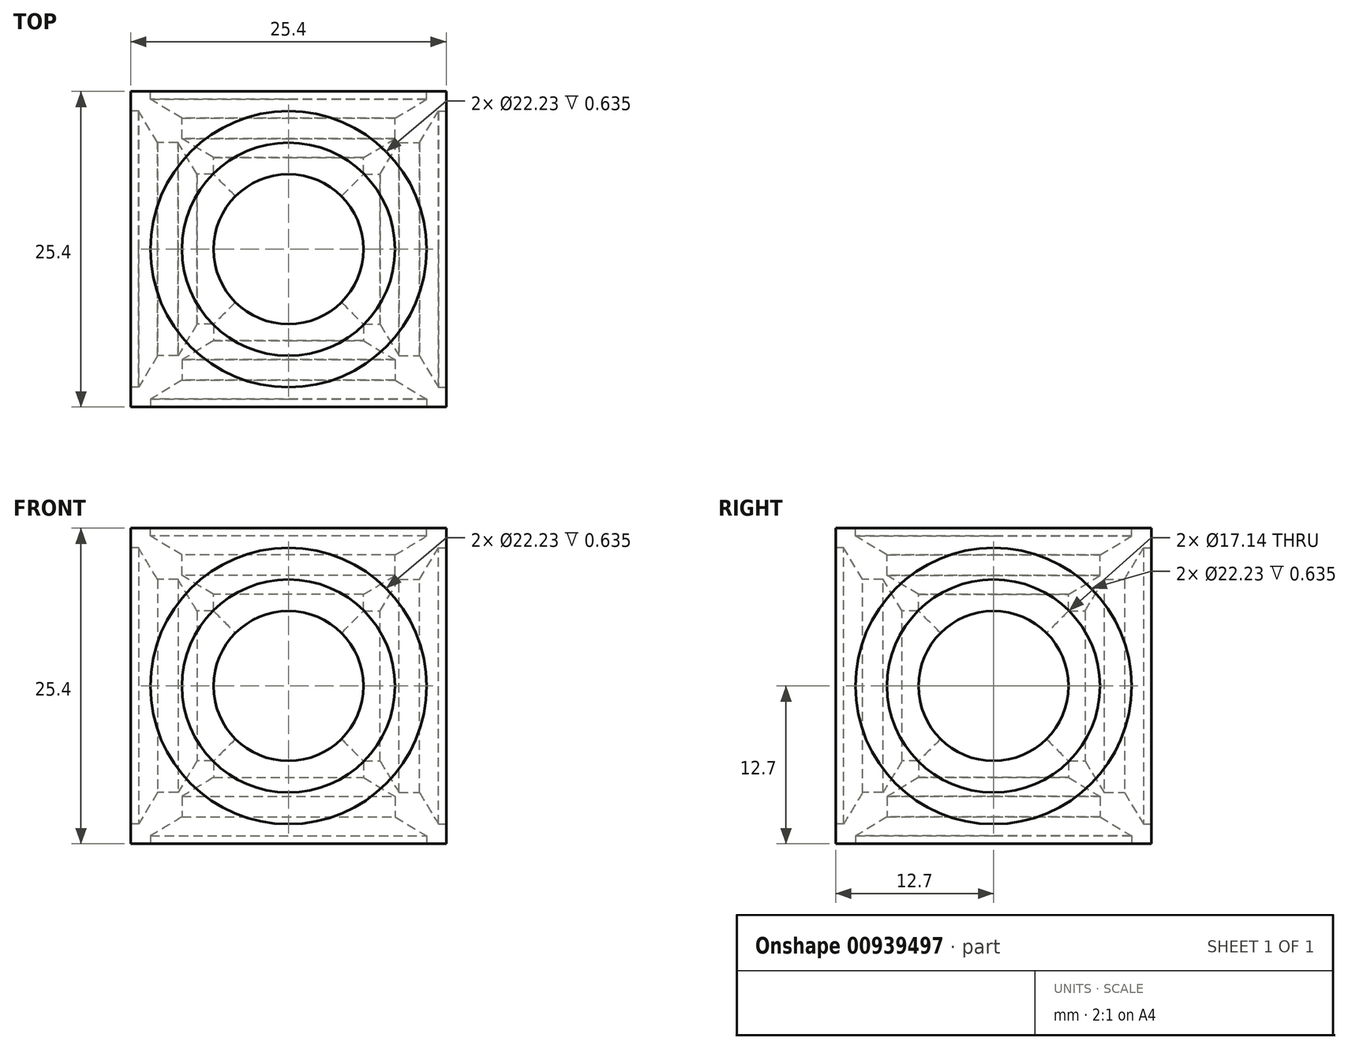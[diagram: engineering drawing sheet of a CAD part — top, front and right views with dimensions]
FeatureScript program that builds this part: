
annotation { "Feature Type Name" : "Feature", "Feature Type Description" : "" }
export const myFeature = defineFeature(function(context is Context, id is Id, definition is map)
    precondition{}
    {
        {
            var Q0;
            Q0=qCreatedBy(makeId("Top.planeOp"),FACE);
            var sketch = newSketch(context, id + "F0", { "sketchPlane" : qUnion([Q0])});
            skLineSegment(sketch, "E0.bottom", {"start": v(12.7, 12.7) * mm, "end": v(-12.7, 12.7) * mm});
            skLineSegment(sketch, "E0.top", {"start": v(12.7, -12.7) * mm, "end": v(-12.7, -12.7) * mm});
            skLineSegment(sketch, "E0.left", {"start": v(12.7, 12.7) * mm, "end": v(12.7, -12.7) * mm});
            skLineSegment(sketch, "E0.right", {"start": v(-12.7, 12.7) * mm, "end": v(-12.7, -12.7) * mm});
            skPoint(sketch, "E0.middle", {"position": v(0, 0) * mm});
            skSolve(sketch);
        }
        {
            var Q0;
            Q0 = qSketchRegion(id + "F0", true);
            extrude(context, id + "F1", {"entities" : qUnion([Q0]), "endBound" : BoundingType.SYMMETRIC, "depth" : 25.4 * mm, "offsetDistance" : 25.4 * mm});
        }
        {
            var Q0;
            Q0=makeQuery(id+"F1.opExtrude","CAP_FACE",FACE,{"disambiguationData":[OSD([sQuery(id+"F0.wireOp",EDGE,"E0.bottom"),sQuery(id+"F0.wireOp",EDGE,"E0.top"),sQuery(id+"F0.wireOp",EDGE,"E0.left"),sQuery(id+"F0.wireOp",EDGE,"E0.right")])],"isStart":false});
            var sketch = newSketch(context, id + "F2", { "sketchPlane" : qUnion([Q0])});
            skPoint(sketch, "E1", {"position": v(0, 0) * mm});
            skSolve(sketch);
        }
        {
            var Q0;
            Q0=sQuery(id+"F2.wireOp",VERTEX,"E1");
            var Q1;
            Q1=makeQuery(id+"F1.opExtrude","SWEPT_BODY",BODY,{"disambiguationData":[OSD([sQuery(id+"F0.wireOp",EDGE,"E0.bottom"),sQuery(id+"F0.wireOp",EDGE,"E0.top"),sQuery(id+"F0.wireOp",EDGE,"E0.left"),sQuery(id+"F0.wireOp",EDGE,"E0.right")])]});
            hole(context, id + "F3", {"style" : HoleStyle.SIMPLE, "endStyle" : HoleEndStyle.THROUGH, "holeDiameter" : 3.17 * mm, "majorDiameter" : 6.35 * mm, "isTappedThrough" : true, "tappedDepth" : 12.7 * mm, "tapClearance" : 3, "locations" : qUnion([Q0]), "scope" : qUnion([Q1])});
        }
        {
            var Q0;
            Q0=makeQuery(id+"F1.opExtrude","SWEPT_FACE",FACE,{"disambiguationData":[OSD([sQuery(id+"F0.wireOp",EDGE,"E0.right")])]});
            var sketch = newSketch(context, id + "F4", { "sketchPlane" : qUnion([Q0])});
            skPoint(sketch, "E2", {"position": v(0, 0) * mm});
            skSolve(sketch);
        }
        {
            var Q0;
            Q0=sQuery(id+"F4.wireOp",VERTEX,"E2");
            var Q1;
            Q1=makeQuery(id+"F1.opExtrude","SWEPT_BODY",BODY,{"disambiguationData":[OSD([sQuery(id+"F0.wireOp",EDGE,"E0.bottom"),sQuery(id+"F0.wireOp",EDGE,"E0.top"),sQuery(id+"F0.wireOp",EDGE,"E0.left"),sQuery(id+"F0.wireOp",EDGE,"E0.right")])]});
            hole(context, id + "F5", {"style" : HoleStyle.SIMPLE, "endStyle" : HoleEndStyle.THROUGH, "holeDiameter" : 3.17 * mm, "majorDiameter" : 6.35 * mm, "isTappedThrough" : true, "tappedDepth" : 12.7 * mm, "tapClearance" : 3, "locations" : qUnion([Q0]), "scope" : qUnion([Q1])});
        }
        {
            var Q0;
            Q0=makeQuery(id+"F1.opExtrude","SWEPT_FACE",FACE,{"disambiguationData":[OSD([sQuery(id+"F0.wireOp",EDGE,"E0.bottom")])]});
            var sketch = newSketch(context, id + "F6", { "sketchPlane" : qUnion([Q0])});
            skPoint(sketch, "E3", {"position": v(0, 0) * mm});
            skSolve(sketch);
        }
        {
            var Q0;
            Q0=sQuery(id+"F6.wireOp",VERTEX,"E3");
            var Q1;
            Q1=makeQuery(id+"F1.opExtrude","SWEPT_BODY",BODY,{"disambiguationData":[OSD([sQuery(id+"F0.wireOp",EDGE,"E0.bottom"),sQuery(id+"F0.wireOp",EDGE,"E0.top"),sQuery(id+"F0.wireOp",EDGE,"E0.left"),sQuery(id+"F0.wireOp",EDGE,"E0.right")])]});
            hole(context, id + "F7", {"style" : HoleStyle.SIMPLE, "endStyle" : HoleEndStyle.THROUGH, "holeDiameter" : 3.17 * mm, "majorDiameter" : 6.35 * mm, "isTappedThrough" : true, "tappedDepth" : 12.7 * mm, "tapClearance" : 3, "locations" : qUnion([Q0]), "scope" : qUnion([Q1])});
        }
        {
            var Q0;
            Q0=makeQuery(id+"F1.opExtrude","CAP_FACE",FACE,{"disambiguationData":[OSD([sQuery(id+"F0.wireOp",EDGE,"E0.bottom"),sQuery(id+"F0.wireOp",EDGE,"E0.top"),sQuery(id+"F0.wireOp",EDGE,"E0.left"),sQuery(id+"F0.wireOp",EDGE,"E0.right")])],"isStart":true});
            var sketch = newSketch(context, id + "F8", { "sketchPlane" : qUnion([Q0])});
            skPoint(sketch, "E4", {"position": v(0, 0) * mm});
            skSolve(sketch);
        }
        {
            var Q0;
            Q0=makeQuery(id+"F1.opExtrude","SWEPT_FACE",FACE,{"disambiguationData":[OSD([sQuery(id+"F0.wireOp",EDGE,"E0.left")])]});
            var sketch = newSketch(context, id + "F9", { "sketchPlane" : qUnion([Q0])});
            skPoint(sketch, "E5", {"position": v(0, 0) * mm});
            skSolve(sketch);
        }
        {
            var Q0;
            Q0=makeQuery(id+"F1.opExtrude","SWEPT_FACE",FACE,{"disambiguationData":[OSD([sQuery(id+"F0.wireOp",EDGE,"E0.top")])]});
            var sketch = newSketch(context, id + "F10", { "sketchPlane" : qUnion([Q0])});
            skPoint(sketch, "E6", {"position": v(0, 0) * mm});
            skSolve(sketch);
        }
        {
            var Q0;
            Q0=sQuery(id+"F8.wireOp",VERTEX,"E4");
            var Q1;
            Q1=sQuery(id+"F6.wireOp",VERTEX,"E3");
            var Q2;
            Q2=sQuery(id+"F10.wireOp",VERTEX,"E6");
            var Q3;
            Q3=sQuery(id+"F4.wireOp",VERTEX,"E2");
            var Q4;
            Q4=sQuery(id+"F9.wireOp",VERTEX,"E5");
            var Q5;
            Q5=sQuery(id+"F2.wireOp",VERTEX,"E1");
            var Q6;
            Q6=makeQuery(id+"F1.opExtrude","SWEPT_BODY",BODY,{"disambiguationData":[OSD([sQuery(id+"F0.wireOp",EDGE,"E0.bottom"),sQuery(id+"F0.wireOp",EDGE,"E0.top"),sQuery(id+"F0.wireOp",EDGE,"E0.left"),sQuery(id+"F0.wireOp",EDGE,"E0.right")])]});
            hole(context, id + "F11", {"style" : HoleStyle.SIMPLE, "endStyle" : HoleEndStyle.BLIND, "holeDiameter" : 17.14 * mm, "majorDiameter" : 6.35 * mm, "holeDepth" : 3.8 * mm, "isTappedThrough" : true, "tappedDepth" : 12.7 * mm, "tapClearance" : 3, "locations" : qUnion([Q0, Q1, Q2, Q3, Q4, Q5]), "scope" : qUnion([Q6])});
        }
        {
            var Q0;
            Q0=sQuery(id+"F9.wireOp",VERTEX,"E5");
            var Q1;
            Q1=sQuery(id+"F2.wireOp",VERTEX,"E1");
            var Q2;
            Q2=sQuery(id+"F10.wireOp",VERTEX,"E6");
            var Q3;
            Q3=sQuery(id+"F8.wireOp",VERTEX,"E4");
            var Q4;
            Q4=sQuery(id+"F4.wireOp",VERTEX,"E2");
            var Q5;
            Q5=sQuery(id+"F6.wireOp",VERTEX,"E3");
            var Q6;
            Q6=makeQuery(id+"F1.opExtrude","SWEPT_BODY",BODY,{"disambiguationData":[OSD([sQuery(id+"F0.wireOp",EDGE,"E0.bottom"),sQuery(id+"F0.wireOp",EDGE,"E0.top"),sQuery(id+"F0.wireOp",EDGE,"E0.left"),sQuery(id+"F0.wireOp",EDGE,"E0.right")])]});
            hole(context, id + "F12", {"style" : HoleStyle.SIMPLE, "endStyle" : HoleEndStyle.BLIND, "holeDiameter" : 22.22 * mm, "majorDiameter" : 6.35 * mm, "holeDepth" : 0.64 * mm, "isTappedThrough" : true, "tappedDepth" : 12.7 * mm, "tapClearance" : 3, "locations" : qUnion([Q0, Q1, Q2, Q3, Q4, Q5]), "scope" : qUnion([Q6])});
        }
        {
            var Q0;
            Q0=sQuery(id+"F4.wireOp",VERTEX,"E2");
            var Q1;
            Q1=sQuery(id+"F8.wireOp",VERTEX,"E4");
            var Q2;
            Q2=sQuery(id+"F10.wireOp",VERTEX,"E6");
            var Q3;
            Q3=sQuery(id+"F9.wireOp",VERTEX,"E5");
            var Q4;
            Q4=sQuery(id+"F6.wireOp",VERTEX,"E3");
            var Q5;
            Q5=sQuery(id+"F2.wireOp",VERTEX,"E1");
            var Q6;
            Q6=makeQuery(id+"F1.opExtrude","SWEPT_BODY",BODY,{"disambiguationData":[OSD([sQuery(id+"F0.wireOp",EDGE,"E0.bottom"),sQuery(id+"F0.wireOp",EDGE,"E0.top"),sQuery(id+"F0.wireOp",EDGE,"E0.left"),sQuery(id+"F0.wireOp",EDGE,"E0.right")])]});
            hole(context, id + "F13", {"style" : HoleStyle.SIMPLE, "endStyle" : HoleEndStyle.BLIND, "holeDiameter" : 12.06 * mm, "majorDiameter" : 6.35 * mm, "holeDepth" : 3.8 * mm, "isTappedThrough" : true, "tappedDepth" : 12.7 * mm, "tapClearance" : 3, "locations" : qUnion([Q0, Q1, Q2, Q3, Q4, Q5]), "scope" : qUnion([Q6])});
        }
    });
